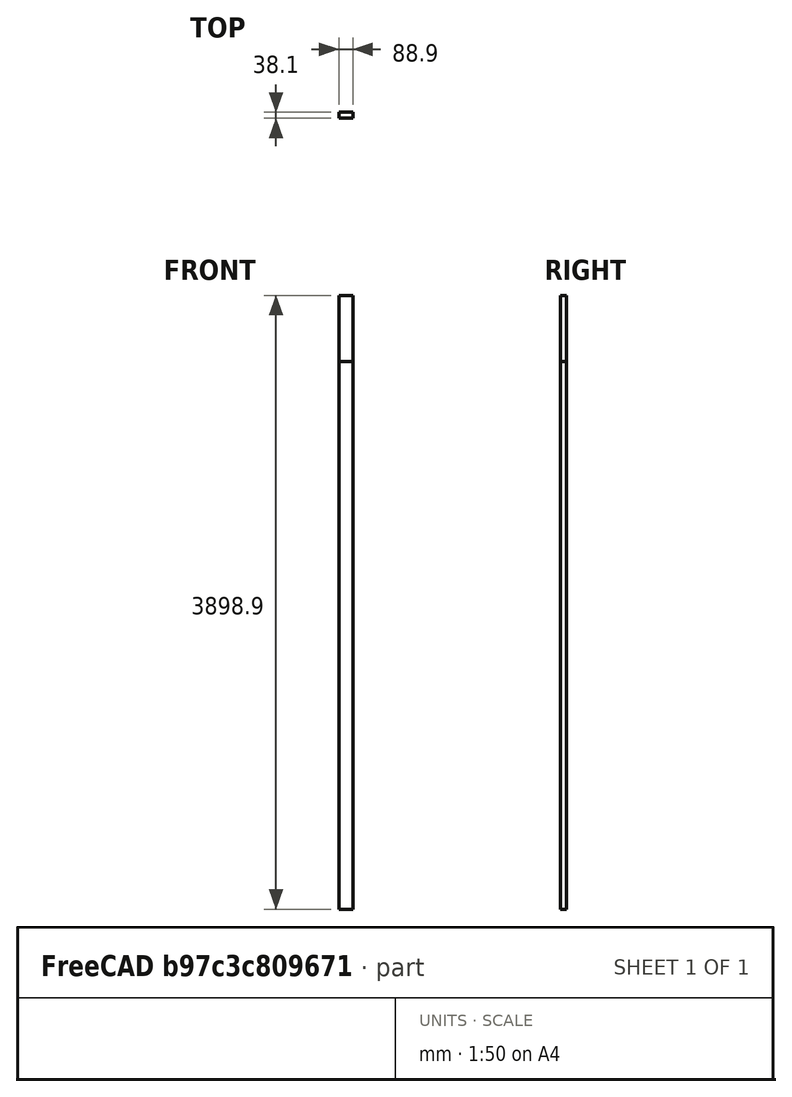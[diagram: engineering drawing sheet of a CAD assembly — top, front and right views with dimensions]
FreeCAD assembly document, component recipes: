
FREECAD ASSEMBLY — COMPONENT RECIPES ("Frame")

This assembly document has 21 components, labeled P0..P20 below (a component is one placed body or linked part). 21 of them carry a construction recipe — the FreeCAD feature program that regenerates the part from scratch, quoted from this document or its linked companion documents; the rest are supplied as boundary geometry only. No exploded tour is included for this assembly.
COMPONENT P0 — recipe-attached ("verticalTimber-Part", modeled in this document).
Construction recipe (the document's own serialized feature program — sketch geometry with constraints, then the solid features built on it; lengths are millimeters unless a unit is written):

FEATURE [Sketcher::SketchObject] Sketch
  ArcFitTolerance = 1e-06
  ExternalBSplineMaxDegree = 5
  ExternalBSplineTolerance = 0.0001
  FixShape = 1
  FullyConstrained = true
  InternalTolerance = 1e-06
  InvalidShape = false
  MakeInternals = false
  MapMode = 2
  TreeRank = 11
  ValidateShape = false
  sketch-geometry (4):
    g0: LineSegment StartX=0 StartY=0 StartZ=0 EndX=88.9 EndY=0 EndZ=0
    g1: LineSegment StartX=88.9 StartY=0 StartZ=0 EndX=88.9 EndY=38.1 EndZ=0
    g2: LineSegment StartX=88.9 StartY=38.1 StartZ=0 EndX=0 EndY=38.1 EndZ=0
    g3: LineSegment StartX=0 StartY=38.1 StartZ=0 EndX=0 EndY=0 EndZ=0
  constraints (11):
    c: Coincident(g0,g1)
    c: Coincident(g1,g2)
    c: Coincident(g2,g3)
    c: Coincident(g3,g0)
    c: Horizontal(g0)
    c: Horizontal(g2)
    c: Vertical(g1)
    c: Vertical(g3)
    c: Coincident(g0,g-1)
    c: DistanceY(g1,g1) = 38.1
    c: DistanceX(g2,g2) = 88.9
FEATURE [PartDesign::Pad] Pad
  AddSubType = 0
  AlongSketchNormal = false
  AutoTaperInnerAngle = true
  CheckUpToFaceLimits = true
  ClaimChildren = false
  Direction = (0,0,1)
  Fit = 0
  FitJoin = 0
  FixShape = 1
  InnerFit = 0
  InnerFitJoin = 0
  InvalidShape = false
  Length = 3479.8
  Length2 = 100
  Linearize = true
  NewSolid = false
  Profile = -> Sketch
  Suppress = false
  TaperInnerAngle = 0
  TaperInnerAngleRev = 0
  TreeRank = 12
  Type = 0
  ValidateShape = false
  _ProfileBasedVersion = 1
FEATURE [PartDesign::Body] Body
  AutoGroupSolids = false
  ClaimAllChildren = false
  ExportMode = 0
  FixShape = 1
  Group = -> [Sketch,Pad]
  InvalidShape = false
  Origin = -> Origin
  Tip = -> Pad
  TreeRank = 10
  ValidateShape = false
  _ExportChildren = -> [Pad]
  _GroupVersion = 1
COMPONENT P1 — same part as P0; its construction recipe is shown at P0.
COMPONENT P2 — same part as P0; its construction recipe is shown at P0.
COMPONENT P3 — same part as P0; its construction recipe is shown at P0.
COMPONENT P4 — same part as P0; its construction recipe is shown at P0.
COMPONENT P5 — same part as P0; its construction recipe is shown at P0.
COMPONENT P6 — same part as P0; its construction recipe is shown at P0.
COMPONENT P7 — same part as P0; its construction recipe is shown at P0.
COMPONENT P8 — same part as P0; its construction recipe is shown at P0.
COMPONENT P9 — same part as P0; its construction recipe is shown at P0.
COMPONENT P10 — same part as P0; its construction recipe is shown at P0.
COMPONENT P11 — same part as P0; its construction recipe is shown at P0.
COMPONENT P12 — same part as P0; its construction recipe is shown at P0.
COMPONENT P13 — same part as P0; its construction recipe is shown at P0.
COMPONENT P14 — same part as P0; its construction recipe is shown at P0.
COMPONENT P15 — same part as P0; its construction recipe is shown at P0.
COMPONENT P16 — same part as P0; its construction recipe is shown at P0.
COMPONENT P17 — same part as P0; its construction recipe is shown at P0.
COMPONENT P18 — same part as P0; its construction recipe is shown at P0.
COMPONENT P19 — recipe-attached ("topTimberPart001", modeled in this document).
Construction recipe (the document's own serialized feature program — sketch geometry with constraints, then the solid features built on it; lengths are millimeters unless a unit is written):

FEATURE [Sketcher::SketchObject] Sketch001
  ArcFitTolerance = 1e-06
  ExternalBSplineMaxDegree = 5
  ExternalBSplineTolerance = 0.0001
  FixShape = 1
  FullyConstrained = true
  InternalTolerance = 1e-06
  InvalidShape = false
  MakeInternals = false
  MapMode = 2
  TreeRank = 11
  ValidateShape = false
  sketch-geometry (4):
    g0: LineSegment StartX=0 StartY=0 StartZ=0 EndX=88.9 EndY=0 EndZ=0
    g1: LineSegment StartX=88.9 StartY=0 StartZ=0 EndX=88.9 EndY=38.1 EndZ=0
    g2: LineSegment StartX=88.9 StartY=38.1 StartZ=0 EndX=0 EndY=38.1 EndZ=0
    g3: LineSegment StartX=0 StartY=38.1 StartZ=0 EndX=0 EndY=0 EndZ=0
  constraints (11):
    c: Coincident(g0,g1)
    c: Coincident(g1,g2)
    c: Coincident(g2,g3)
    c: Coincident(g3,g0)
    c: Horizontal(g0)
    c: Horizontal(g2)
    c: Vertical(g1)
    c: Vertical(g3)
    c: Coincident(g0,g-1)
    c: DistanceY(g1,g1) = 38.1
    c: DistanceX(g2,g2) = 88.9
FEATURE [PartDesign::Pad] Pad001
  AddSubType = 0
  AlongSketchNormal = false
  AutoTaperInnerAngle = true
  CheckUpToFaceLimits = true
  ClaimChildren = false
  Direction = (0,0,1)
  Fit = 0
  FitJoin = 0
  FixShape = 1
  InnerFit = 0
  InnerFitJoin = 0
  InvalidShape = false
  Length = 3479.8
  Length2 = 100
  Linearize = true
  NewSolid = false
  Profile = -> Sketch001
  Suppress = false
  TaperInnerAngle = 0
  TaperInnerAngleRev = 0
  TreeRank = 12
  Type = 0
  ValidateShape = false
  _ProfileBasedVersion = 1
FEATURE [PartDesign::Body] Body001
  AutoGroupSolids = false
  ClaimAllChildren = false
  ExportMode = 0
  FixShape = 1
  Group = -> [Sketch001,Pad001]
  InvalidShape = false
  Origin = -> Origin002
  Tip = -> Pad001
  TreeRank = 16
  ValidateShape = false
  _ExportChildren = -> [Pad001]
  _GroupVersion = 1
COMPONENT P20 — recipe-attached ("Frame-backTimber-Part", modeled in this document).
Construction recipe (the document's own serialized feature program — sketch geometry with constraints, then the solid features built on it; lengths are millimeters unless a unit is written):

FEATURE [Sketcher::SketchObject] Sketch002
  ArcFitTolerance = 1e-06
  ExternalBSplineMaxDegree = 5
  ExternalBSplineTolerance = 0.0001
  FixShape = 1
  FullyConstrained = true
  InternalTolerance = 1e-06
  InvalidShape = false
  MakeInternals = false
  MapMode = 2
  TreeRank = 32
  ValidateShape = false
  sketch-geometry (4):
    g0: LineSegment StartX=0 StartY=0 StartZ=0 EndX=88.9 EndY=0 EndZ=0
    g1: LineSegment StartX=88.9 StartY=0 StartZ=0 EndX=88.9 EndY=38.1 EndZ=0
    g2: LineSegment StartX=88.9 StartY=38.1 StartZ=0 EndX=0 EndY=38.1 EndZ=0
    g3: LineSegment StartX=0 StartY=38.1 StartZ=0 EndX=0 EndY=0 EndZ=0
  constraints (11):
    c: Coincident(g0,g1)
    c: Coincident(g1,g2)
    c: Coincident(g2,g3)
    c: Coincident(g3,g0)
    c: Horizontal(g0)
    c: Horizontal(g2)
    c: Vertical(g1)
    c: Vertical(g3)
    c: Coincident(g0,g-1)
    c: DistanceY(g1,g1) = 38.1
    c: DistanceX(g0,g0) = 88.9
FEATURE [PartDesign::Pad] Pad002
  AddSubType = 0
  AlongSketchNormal = false
  AutoTaperInnerAngle = true
  CheckUpToFaceLimits = true
  ClaimChildren = false
  Direction = (0,0,1)
  Fit = 0
  FitJoin = 0
  FixShape = 1
  InnerFit = 0
  InnerFitJoin = 0
  InvalidShape = false
  Length = 3898.9
  Length2 = 100
  Linearize = true
  NewSolid = false
  Profile = -> Sketch002
  Suppress = false
  TaperInnerAngle = 0
  TaperInnerAngleRev = 0
  TreeRank = 33
  Type = 0
  ValidateShape = false
  _ProfileBasedVersion = 1
FEATURE [PartDesign::Body] Body002
  AutoGroupSolids = false
  ClaimAllChildren = false
  ExportMode = 0
  FixShape = 1
  Group = -> [Sketch002,Pad002]
  InvalidShape = false
  Origin = -> Origin005
  Tip = -> Pad002
  TreeRank = 31
  ValidateShape = false
  _ExportChildren = -> [Pad002]
  _GroupVersion = 1
PROVENANCE & LICENSES
A FreeCAD (.FCStd) document from a public repository crawl; recipes are the document's own serialized feature recipes (and, for linked parts, companion documents' recipes).
License: agpl-3.0.
